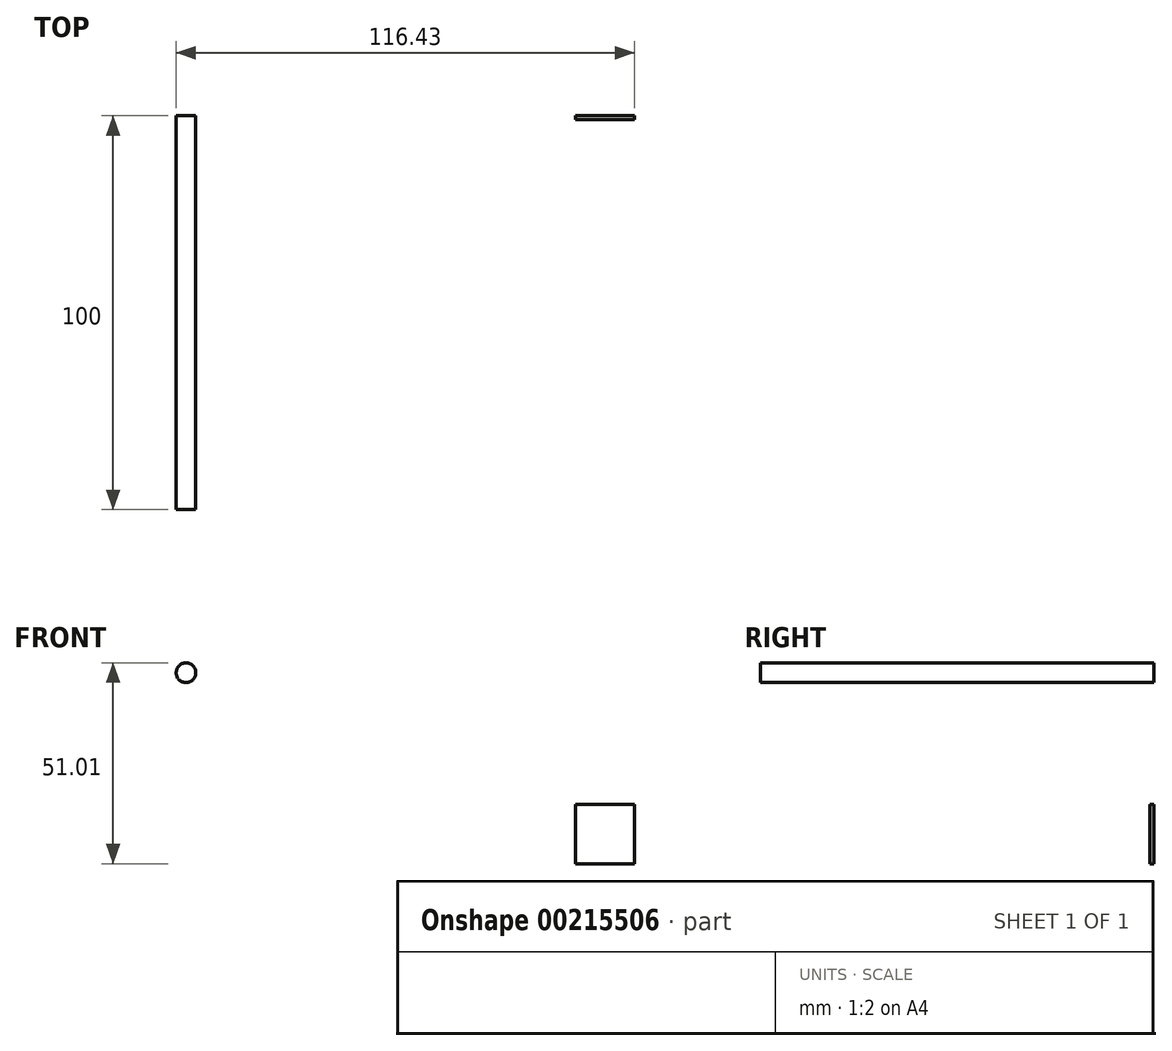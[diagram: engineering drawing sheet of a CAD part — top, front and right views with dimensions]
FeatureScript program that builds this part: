
annotation { "Feature Type Name" : "Feature", "Feature Type Description" : "" }
export const myFeature = defineFeature(function(context is Context, id is Id, definition is map)
    precondition{}
    {
        {
            var Q0;
            Q0=qCreatedBy(makeId("Front.planeOp"),FACE);
            var sketch = newSketch(context, id + "F0", { "sketchPlane" : qUnion([Q0])});
            skLineSegment(sketch, "E0.bottom", {"start": v(-7.5, -7.5) * mm, "end": v(7.5, -7.5) * mm});
            skLineSegment(sketch, "E0.top", {"start": v(-7.5, 7.5) * mm, "end": v(7.5, 7.5) * mm});
            skLineSegment(sketch, "E0.left", {"start": v(-7.5, -7.5) * mm, "end": v(-7.5, 7.5) * mm});
            skLineSegment(sketch, "E0.right", {"start": v(7.5, -7.5) * mm, "end": v(7.5, 7.5) * mm});
            skPoint(sketch, "E0.middle", {"position": v(0, 0) * mm});
            skSolve(sketch);
        }
        {
            var Q0;
            Q0=makeQuery(id+"F0.imprint","IMPRINT",FACE,{"disambiguationData":[TD([[makeQuery(id+"F0.imprint","IMPRINT",EDGE,{"derivedFrom":sQuery(id+"F0.wireOp",EDGE,"E0.bottom")}),1.0]])]});
            extrude(context, id + "F1", {"entities" : qUnion([Q0]), "depth" : 1 * mm});
        }
        {
            var Q0;
            Q0=qCreatedBy(makeId("Front.planeOp"),FACE);
            var sketch = newSketch(context, id + "F2", { "sketchPlane" : qUnion([Q0])});
            skCircle(sketch, "E1", {"center": v(-106.43, 41) * mm, "radius": 2.5 * mm});
            skSolve(sketch);
        }
        {
            var Q0;
            Q0=makeQuery(id+"F2.imprint","IMPRINT",FACE,{"disambiguationData":[TD([[makeQuery(id+"F2.imprint","IMPRINT",EDGE,{"derivedFrom":sQuery(id+"F2.wireOp",EDGE,"E1")}),1.0]])]});
            extrude(context, id + "F3", {"entities" : qUnion([Q0]), "depth" : 100 * mm});
        }
    });
